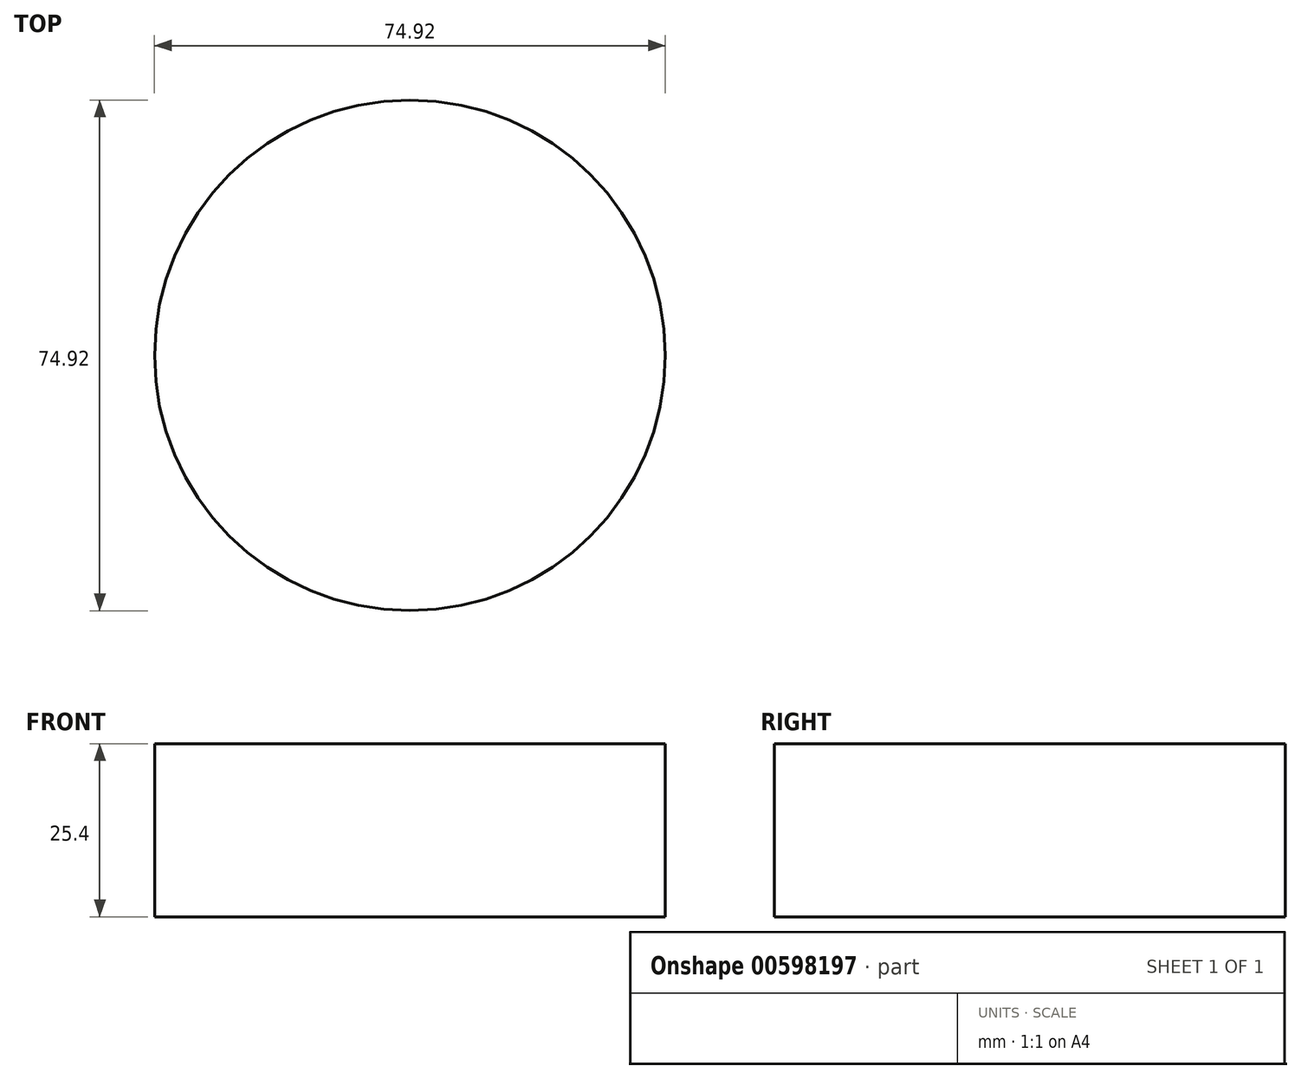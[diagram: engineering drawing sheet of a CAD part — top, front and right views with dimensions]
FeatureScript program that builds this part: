
annotation { "Feature Type Name" : "Feature", "Feature Type Description" : "" }
export const myFeature = defineFeature(function(context is Context, id is Id, definition is map)
    precondition{}
    {
        {
            var Q0;
            Q0=qCreatedBy(makeId("Top.planeOp"),FACE);
            var sketch = newSketch(context, id + "F0", { "sketchPlane" : qUnion([Q0])});
            skCircle(sketch, "E0", {"center": v(-25.72, 34.14) * mm, "radius": 37.46 * mm});
            skSolve(sketch);
        }
        {
            var Q0;
            Q0 = qSketchRegion(id + "F0", true);
            extrude(context, id + "F1", {"entities" : qUnion([Q0]), "depth" : 25.4 * mm, "offsetDistance" : 25.4 * mm});
        }
    });
